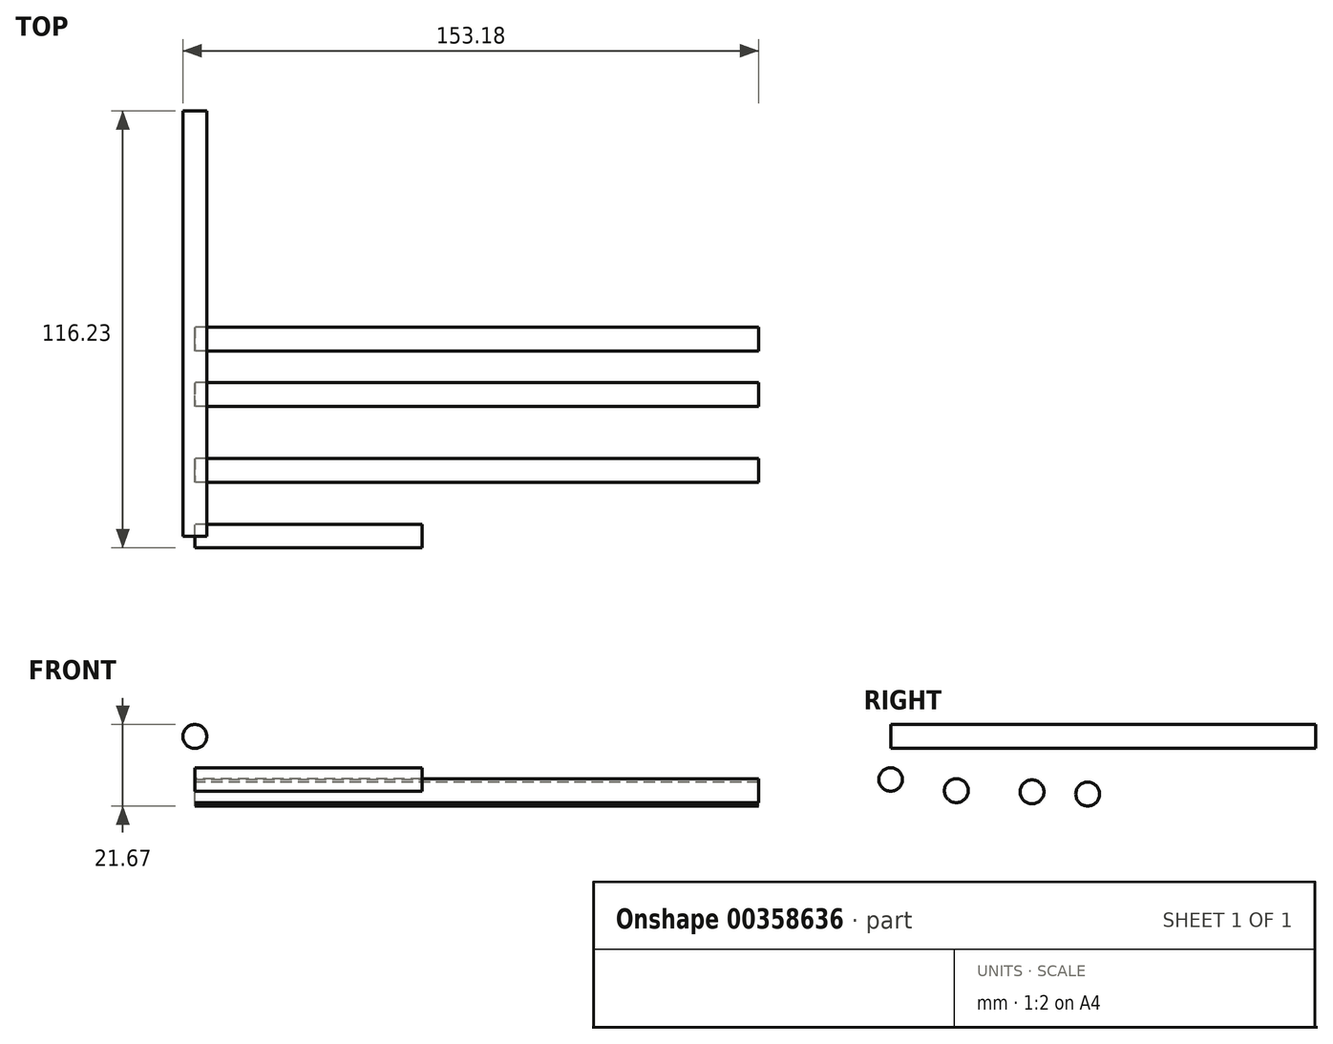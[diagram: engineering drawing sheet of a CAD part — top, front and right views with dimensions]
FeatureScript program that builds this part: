
annotation { "Feature Type Name" : "Feature", "Feature Type Description" : "" }
export const myFeature = defineFeature(function(context is Context, id is Id, definition is map)
    precondition{}
    {
        {
            var Q0;
            Q0=qCreatedBy(makeId("Front.planeOp"),FACE);
            var sketch = newSketch(context, id + "F0", { "sketchPlane" : qUnion([Q0])});
            skCircle(sketch, "E0", {"center": v(0, 0) * mm, "radius": 3.17 * mm});
            skSolve(sketch);
        }
        {
            var Q0;
            Q0 = qSketchRegion(id + "F0", true);
            extrude(context, id + "F1", {"entities" : qUnion([Q0]), "oppositeDirection" : true, "depth" : (200 - 86.9) * mm, "offsetDistance" : 25 * mm});
        }
        {
            var Q0;
            Q0=qCreatedBy(makeId("Right.planeOp"),FACE);
            var sketch = newSketch(context, id + "F2", { "sketchPlane" : qUnion([Q0])});
            skCircle(sketch, "E1", {"center": v(0, -11.43) * mm, "radius": 3.12 * mm});
            skSolve(sketch);
        }
        {
            var Q0;
            Q0 = qSketchRegion(id + "F2", true);
            extrude(context, id + "F3", {"entities" : qUnion([Q0]), "depth" : 60.42 * mm, "offsetDistance" : 25 * mm});
        }
        {
            var Q0;
            Q0=qCreatedBy(makeId("Right.planeOp"),FACE);
            var sketch = newSketch(context, id + "F4", { "sketchPlane" : qUnion([Q0])});
            skCircle(sketch, "E2", {"center": v(17.48, -14.4) * mm, "radius": 3.17 * mm});
            skSolve(sketch);
        }
        {
            var Q0;
            Q0 = qSketchRegion(id + "F4", true);
            extrude(context, id + "F5", {"entities" : qUnion([Q0]), "depth" : 150 * mm, "offsetDistance" : 25 * mm});
        }
        {
            var Q0;
            Q0=qCreatedBy(makeId("Right.planeOp"),FACE);
            var sketch = newSketch(context, id + "F6", { "sketchPlane" : qUnion([Q0])});
            skCircle(sketch, "E3", {"center": v(37.6, -14.74) * mm, "radius": 3.17 * mm});
            skSolve(sketch);
        }
        {
            var Q0;
            Q0 = qSketchRegion(id + "F6", true);
            extrude(context, id + "F7", {"entities" : qUnion([Q0]), "depth" : 150 * mm, "offsetDistance" : 25 * mm});
        }
        {
            var Q0;
            Q0=qCreatedBy(makeId("Right.planeOp"),FACE);
            var sketch = newSketch(context, id + "F8", { "sketchPlane" : qUnion([Q0])});
            skCircle(sketch, "E4", {"center": v(52.43, -15.32) * mm, "radius": 3.17 * mm});
            skSolve(sketch);
        }
        {
            var Q0;
            Q0 = qSketchRegion(id + "F8", true);
            extrude(context, id + "F9", {"entities" : qUnion([Q0]), "depth" : 150 * mm, "offsetDistance" : 25 * mm});
        }
    });
